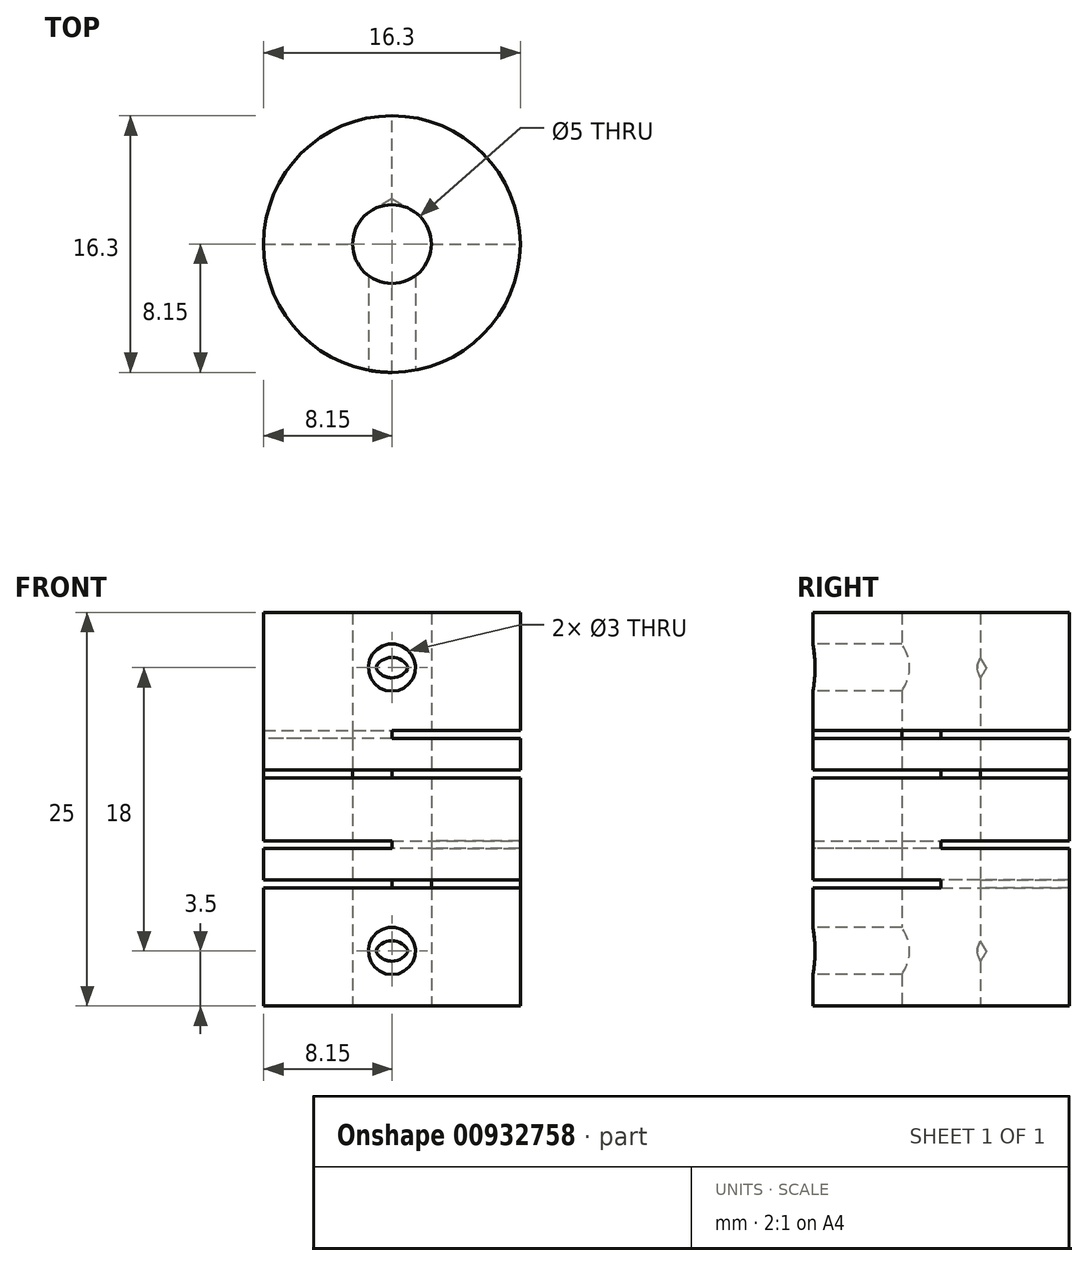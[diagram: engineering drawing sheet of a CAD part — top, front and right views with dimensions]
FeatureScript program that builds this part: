
annotation { "Feature Type Name" : "Feature", "Feature Type Description" : "" }
export const myFeature = defineFeature(function(context is Context, id is Id, definition is map)
    precondition{}
    {
        {
            assignVariable(context, id + "F0", {"name" : "outer_diam", "anyValue" : 16.3});
        }
        {
            var Q0;
            Q0=qCreatedBy(makeId("Top.planeOp"),FACE);
            var sketch = newSketch(context, id + "F1", { "sketchPlane" : qUnion([Q0])});
            skCircle(sketch, "E0", {"center": v(0, 0) * mm, "radius": 8.15 * mm});
            skCircle(sketch, "E1", {"center": v(0, 0) * mm, "radius": 2.5 * mm});
            skSolve(sketch);
        }
        {
            var Q0;
            Q0=makeQuery(id+"F1.imprint","IMPRINT",FACE,{"disambiguationData":[TD([[makeQuery(id+"F1.imprint","IMPRINT",EDGE,{"derivedFrom":sQuery(id+"F1.wireOp",EDGE,"E0")}),1.0]])]});
            extrude(context, id + "F2", {"entities" : qUnion([Q0]), "endBound" : BoundingType.SYMMETRIC, "depth" : 25 * mm, "offsetDistance" : 25 * mm});
        }
        {
            var Q0;
            Q0=qCreatedBy(makeId("Front.planeOp"),FACE);
            var sketch = newSketch(context, id + "F3", { "sketchPlane" : qUnion([Q0])});
            skLineSegment(sketch, "E2", {"start": v(-8.5, 5) * mm, "end": v(-1.6, 5) * mm});
            skLineSegment(sketch, "E3", {"start": v(-1.6, 5) * mm, "end": v(-1.6, 4.5) * mm});
            skLineSegment(sketch, "E4", {"start": v(-1.6, 4.5) * mm, "end": v(-8.5, 4.5) * mm});
            skLineSegment(sketch, "E5", {"start": v(-8.5, 4.5) * mm, "end": v(-8.5, 5) * mm});
            skLineSegment(sketch, "E6", {"start": v(1.64, -4.5) * mm, "end": v(8.67, -4.5) * mm});
            skLineSegment(sketch, "E7", {"start": v(8.67, -4.5) * mm, "end": v(8.67, -5) * mm});
            skLineSegment(sketch, "E8", {"start": v(8.67, -5) * mm, "end": v(1.64, -5) * mm});
            skLineSegment(sketch, "E9", {"start": v(1.64, -5) * mm, "end": v(1.64, -4.5) * mm});
            skPoint(sketch, "E10", {"position": v(0, 9) * mm});
            skPoint(sketch, "E11", {"position": v(0, -9) * mm});
            skSolve(sketch);
        }
        {
            var Q0;
            Q0=makeQuery(id+"F3.imprint","IMPRINT",FACE,{"disambiguationData":[TD([[makeQuery(id+"F3.imprint","IMPRINT",EDGE,{"derivedFrom":sQuery(id+"F3.wireOp",EDGE,"E2")}),-1.0]])]});
            var Q1;
            Q1=makeQuery(id+"F2.opExtrude","SWEPT_FACE",FACE,{"disambiguationData":[OSD([sQuery(id+"F1.wireOp",EDGE,"E1")])]});
            revolve(context, id + "F4", {"operationType" : NewBodyOperationType.REMOVE, "surfaceOperationType" : NewSurfaceOperationType.NEW, "entities" : qUnion([Q0]), "axis" : qUnion([Q1]), "revolveType" : RevolveType.ONE_DIRECTION, "oppositeDirection" : true, "angle" : 270 * degree});
        }
        {
            var Q0;
            Q0=makeQuery(id+"F3.imprint","IMPRINT",FACE,{"disambiguationData":[TD([[makeQuery(id+"F3.imprint","IMPRINT",EDGE,{"derivedFrom":sQuery(id+"F3.wireOp",EDGE,"E6")}),-1.0]])]});
            var Q1;
            Q1=makeQuery(id+"F2.opExtrude","SWEPT_FACE",FACE,{"disambiguationData":[OSD([sQuery(id+"F1.wireOp",EDGE,"E1")])]});
            revolve(context, id + "F5", {"operationType" : NewBodyOperationType.REMOVE, "surfaceOperationType" : NewSurfaceOperationType.NEW, "entities" : qUnion([Q0]), "axis" : qUnion([Q1]), "revolveType" : RevolveType.ONE_DIRECTION, "oppositeDirection" : true, "angle" : 270 * degree});
        }
        {
            var Q0;
            Q0=qCreatedBy(makeId("Right.planeOp"),FACE);
            var sketch = newSketch(context, id + "F6", { "sketchPlane" : qUnion([Q0])});
            skLineSegment(sketch, "E12", {"start": v(-8.56, -2) * mm, "end": v(-2, -2) * mm});
            skLineSegment(sketch, "E13", {"start": v(-2, -2) * mm, "end": v(-2, -2.5) * mm});
            skLineSegment(sketch, "E14", {"start": v(-2, -2.5) * mm, "end": v(-8.56, -2.5) * mm});
            skLineSegment(sketch, "E15", {"start": v(-8.56, -2.5) * mm, "end": v(-8.56, -2) * mm});
            skLineSegment(sketch, "E16.MirrorCS", {"start": v(2.1, 2) * mm, "end": v(8.6, 2) * mm});
            skLineSegment(sketch, "E17.MirrorCS", {"start": v(8.6, 2.5) * mm, "end": v(2.1, 2.5) * mm});
            skLineSegment(sketch, "E18.MirrorCS", {"start": v(2.1, 2.5) * mm, "end": v(2.1, 2) * mm});
            skLineSegment(sketch, "E19.MirrorCS", {"start": v(8.6, 2) * mm, "end": v(8.6, 2.5) * mm});
            skSolve(sketch);
        }
        {
            var Q0;
            Q0=makeQuery(id+"F6.imprint","IMPRINT",FACE,{"disambiguationData":[TD([[makeQuery(id+"F6.imprint","IMPRINT",EDGE,{"derivedFrom":sQuery(id+"F6.wireOp",EDGE,"E12")}),-1.0]])]});
            var Q1;
            Q1=makeQuery(id+"F2.opExtrude","SWEPT_FACE",FACE,{"disambiguationData":[OSD([sQuery(id+"F1.wireOp",EDGE,"E1")])]});
            revolve(context, id + "F7", {"operationType" : NewBodyOperationType.REMOVE, "surfaceOperationType" : NewSurfaceOperationType.NEW, "entities" : qUnion([Q0]), "axis" : qUnion([Q1]), "revolveType" : RevolveType.ONE_DIRECTION, "oppositeDirection" : true, "angle" : 270 * degree});
        }
        {
            var Q0;
            Q0=makeQuery(id+"F6.imprint","IMPRINT",FACE,{"disambiguationData":[TD([[makeQuery(id+"F6.imprint","IMPRINT",EDGE,{"derivedFrom":sQuery(id+"F6.wireOp",EDGE,"E16.MirrorCS")}),1.0]])]});
            var Q1;
            Q1=makeQuery(id+"F2.opExtrude","SWEPT_FACE",FACE,{"disambiguationData":[OSD([sQuery(id+"F1.wireOp",EDGE,"E1")])]});
            revolve(context, id + "F8", {"operationType" : NewBodyOperationType.REMOVE, "surfaceOperationType" : NewSurfaceOperationType.NEW, "entities" : qUnion([Q0]), "axis" : qUnion([Q1]), "revolveType" : RevolveType.ONE_DIRECTION, "oppositeDirection" : true, "angle" : 270 * degree});
        }
        {
            var Q0;
            Q0=qCreatedBy(makeId("Front.planeOp"),FACE);
            cPlane(context, id + "F9", {"entities" : qUnion([Q0]), "cplaneType" : CPlaneType.OFFSET, "offset" : (getVariable(context, 'outer_diam') / 2) * mm, "width" : 150 * mm, "height" : 150 * mm});
        }
        {
            var Q0;
            Q0=qCreatedBy(id+"F9.planeOp",FACE);
            var sketch = newSketch(context, id + "F10", { "sketchPlane" : qUnion([Q0])});
            skPoint(sketch, "E20", {"position": v(0, 9) * mm});
            skPoint(sketch, "E21", {"position": v(0, -9) * mm});
            skSolve(sketch);
        }
        {
            var Q0;
            Q0=sQuery(id+"F10.wireOp",VERTEX,"E20");
            var Q1;
            Q1=sQuery(id+"F10.wireOp",VERTEX,"E21");
            var Q2;
            Q2=makeQuery(id+"F2.opExtrude","SWEPT_BODY",BODY,{"disambiguationData":[OSD([sQuery(id+"F1.wireOp",EDGE,"E0"),sQuery(id+"F1.wireOp",EDGE,"E1")])]});
            hole(context, id + "F11", {"style" : HoleStyle.SIMPLE, "endStyle" : HoleEndStyle.BLIND, "holeDiameter" : 3 * mm, "majorDiameter" : 5 * mm, "holeDepth" : 10 * mm, "isTappedThrough" : true, "tappedDepth" : 12 * mm, "tapClearance" : 3, "locations" : qUnion([Q0, Q1]), "scope" : qUnion([Q2])});
        }
    });
